# Revit family: Faucet-Wall_Mount-Handle-KALLISTA-Vice-P34893-1
name_source: partatom
category: Plumbing Fixtures
units: mm (PartAtom-declared; Revit-internal decimal feet)

## family parameters
Cut with Voids When Loaded = No
Host = Face
OmniClass Number = 23.31.11.00
OmniClass Title = Faucets
Part Type = Normal
Room Calculation Point = No
Round Connector Dimension = Use Diameter
Shared = No

## types (4) — shared parameters
ADA Compliant = No
Assembly Code = D2010
CW Connection = Yes
Cold Water Inlet = Cold Water Inlet
Date Modified = 04/26/2024
Default Elevation = 36"
Description = Wall Mount Bath Faucet Handles, Wheel
Drain Included = No
Flow Rate = 0 GPM
HW Connection = Yes
Handle Clearance = 3 3/16"
Height = 2 15/16"
Hot Water Inlet = Hot Water Inlet
Length = 2 3/16"
Manufacturer = Kallista Co.
Master Format 2014 = 22 41 39
Master Format 2014 Name = Residential Faucets, Supplies, and Trim
Material = Premium Metal Construction
Pressure = 0.00 psi
Product Name = Vice
URL = https://www.kallista.com
Vent Connection = No
Waste Connection = No
Waste Water Outlet = Waste Water Outlet
WaterSense Certified = No
Width = 5 7/8"

## per-type parameters (varying)
| type | Finish | Model | Type |
| AF-French Gold | Kallista-Metal-AF-French_Gold | P34893-00-AF | 1 |
| SN-Polished Nickel | Kallista-Metal-SN-Polished_Nickel | P34893-00-SN | 2 |
| CP-Chrome | Kallista-Metal-CP-Chrome | P34893-00-CP | 3 |
| BGP | Kallista-Metal-BGP | P34893-00-BGP | 4 |

## geometry (parser evidence)
native form markers: Sweep x5
no freeform markers — native parametric forms only
